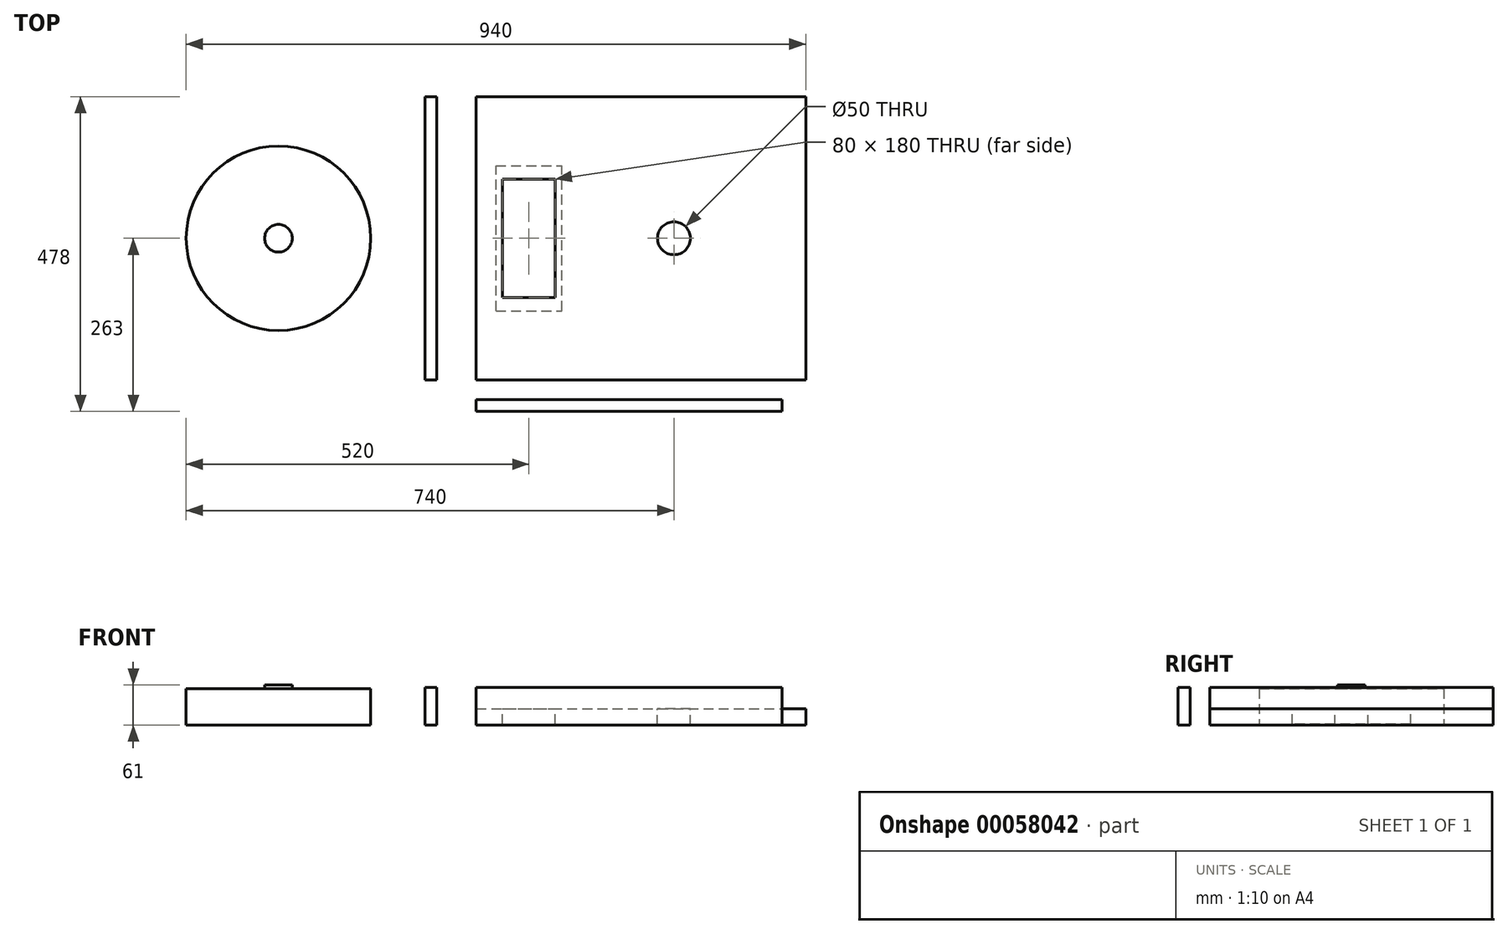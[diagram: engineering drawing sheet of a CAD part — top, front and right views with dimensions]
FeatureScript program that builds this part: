
annotation { "Feature Type Name" : "Feature", "Feature Type Description" : "" }
export const myFeature = defineFeature(function(context is Context, id is Id, definition is map)
    precondition{}
    {
        {
            var Q0;
            Q0=qCreatedBy(makeId("Top.planeOp"),FACE);
            var sketch = newSketch(context, id + "F0", { "sketchPlane" : qUnion([Q0])});
            skLineSegment(sketch, "E0.bottom", {"start": v(0, 0) * mm, "end": v(500, 0) * mm});
            skLineSegment(sketch, "E0.top", {"start": v(0, 430) * mm, "end": v(500, 430) * mm});
            skLineSegment(sketch, "E0.left", {"start": v(0, 0) * mm, "end": v(0, 430) * mm});
            skLineSegment(sketch, "E0.right", {"start": v(500, 0) * mm, "end": v(500, 430) * mm});
            skSolve(sketch);
        }
        {
            var Q0;
            Q0=makeQuery(id+"F0.imprint","IMPRINT",FACE,{"disambiguationData":[TD([[makeQuery(id+"F0.imprint","IMPRINT",EDGE,{"derivedFrom":sQuery(id+"F0.wireOp",EDGE,"E0.bottom")}),1.0]])]});
            extrude(context, id + "F1", {"entities" : qUnion([Q0]), "depth" : 25 * mm});
        }
        {
            var Q0;
            Q0=makeQuery(id+"F1.opExtrude","CAP_FACE",FACE,{"disambiguationData":[OSD([sQuery(id+"F0.wireOp",EDGE,"E0.bottom"),sQuery(id+"F0.wireOp",EDGE,"E0.top"),sQuery(id+"F0.wireOp",EDGE,"E0.left"),sQuery(id+"F0.wireOp",EDGE,"E0.right")])],"isStart":false});
            var sketch = newSketch(context, id + "F2", { "sketchPlane" : qUnion([Q0])});
            skLineSegment(sketch, "E1.bottom", {"start": v(40, 305) * mm, "end": v(120, 305) * mm});
            skLineSegment(sketch, "E1.top", {"start": v(40, 125) * mm, "end": v(120, 125) * mm});
            skLineSegment(sketch, "E1.left", {"start": v(40, 305) * mm, "end": v(40, 125) * mm});
            skLineSegment(sketch, "E1.right", {"start": v(120, 305) * mm, "end": v(120, 125) * mm});
            skCircle(sketch, "E2", {"center": v(300, 215) * mm, "radius": 25 * mm});
            skSolve(sketch);
        }
        {
            var Q0;
            Q0=qCreatedBy(makeId("Top.planeOp"),FACE);
            var sketch = newSketch(context, id + "F3", { "sketchPlane" : qUnion([Q0])});
            skCircle(sketch, "E3", {"center": v(-300, 215) * mm, "radius": 140 * mm});
            skSolve(sketch);
        }
        {
            var Q0;
            Q0=makeQuery(id+"F3.imprint","IMPRINT",FACE,{"disambiguationData":[TD([[makeQuery(id+"F3.imprint","IMPRINT",EDGE,{"derivedFrom":sQuery(id+"F3.wireOp",EDGE,"E3")}),1.0]])]});
            extrude(context, id + "F4", {"entities" : qUnion([Q0]), "depth" : 55 * mm});
        }
        {
            var Q0;
            Q0=makeQuery(id+"F4.opExtrude","CAP_FACE",FACE,{"disambiguationData":[OSD([sQuery(id+"F3.wireOp",EDGE,"E3")])],"isStart":false});
            var sketch = newSketch(context, id + "F5", { "sketchPlane" : qUnion([Q0])});
            skCircle(sketch, "E4", {"center": v(-300, 215) * mm, "radius": 21 * mm});
            skSolve(sketch);
        }
        {
            var Q0;
            Q0=makeQuery(id+"F5.imprint","IMPRINT",FACE,{"disambiguationData":[TD([[makeQuery(id+"F5.imprint","IMPRINT",EDGE,{"derivedFrom":sQuery(id+"F5.wireOp",EDGE,"E4")}),1.0]])]});
            extrude(context, id + "F6", {"entities" : qUnion([Q0]), "operationType" : NewBodyOperationType.ADD, "depth" : 6 * mm});
        }
        {
            var Q0;
            Q0=qCreatedBy(makeId("Top.planeOp"),FACE);
            var sketch = newSketch(context, id + "F7", { "sketchPlane" : qUnion([Q0])});
            skLineSegment(sketch, "E5.bottom", {"start": v(-78, 430) * mm, "end": v(-60, 430) * mm});
            skLineSegment(sketch, "E5.top", {"start": v(-78, 0) * mm, "end": v(-60, 0) * mm});
            skLineSegment(sketch, "E5.left", {"start": v(-78, 430) * mm, "end": v(-78, 0) * mm});
            skLineSegment(sketch, "E5.right", {"start": v(-60, 430) * mm, "end": v(-60, 0) * mm});
            skLineSegment(sketch, "E6.bottom", {"start": v(0, -30) * mm, "end": v(464, -30) * mm});
            skLineSegment(sketch, "E6.top", {"start": v(0, -48) * mm, "end": v(464, -48) * mm});
            skLineSegment(sketch, "E6.left", {"start": v(0, -30) * mm, "end": v(0, -48) * mm});
            skLineSegment(sketch, "E6.right", {"start": v(464, -30) * mm, "end": v(464, -48) * mm});
            skSolve(sketch);
        }
        {
            var Q0;
            Q0 = qSketchRegion(id + "F7", true);
            extrude(context, id + "F8", {"entities" : qUnion([Q0]), "depth" : 57 * mm});
        }
        {
            var Q0;
            Q0 = qSketchRegion(id + "F2", true);
            extrude(context, id + "F9", {"entities" : qUnion([Q0]), "operationType" : NewBodyOperationType.REMOVE, "endBound" : BoundingType.THROUGH_ALL, "oppositeDirection" : true, "depth" : 25 * mm});
        }
        {
            var Q0;
            Q0=makeQuery(id+"F1.opExtrude","CAP_FACE",FACE,{"disambiguationData":[OSD([sQuery(id+"F0.wireOp",EDGE,"E0.bottom"),sQuery(id+"F0.wireOp",EDGE,"E0.top"),sQuery(id+"F0.wireOp",EDGE,"E0.left"),sQuery(id+"F0.wireOp",EDGE,"E0.right")])],"isStart":true});
            var sketch = newSketch(context, id + "F10", { "sketchPlane" : qUnion([Q0])});
            skLineSegment(sketch, "E7.bottom", {"start": v(30, -105) * mm, "end": v(130, -105) * mm});
            skLineSegment(sketch, "E7.top", {"start": v(30, -325) * mm, "end": v(130, -325) * mm});
            skLineSegment(sketch, "E7.left", {"start": v(30, -105) * mm, "end": v(30, -325) * mm});
            skLineSegment(sketch, "E7.right", {"start": v(130, -105) * mm, "end": v(130, -325) * mm});
            skSolve(sketch);
        }
        {
            var Q0;
            Q0=makeQuery(id+"F10.imprint","IMPRINT",FACE,{"disambiguationData":[TD([[makeQuery(id+"F10.imprint","IMPRINT",EDGE,{"derivedFrom":sQuery(id+"F10.wireOp",EDGE,"E7.bottom")}),-1.0]])]});
            extrude(context, id + "F11", {"entities" : qUnion([Q0]), "operationType" : NewBodyOperationType.REMOVE, "oppositeDirection" : true, "depth" : 1.5 * mm});
        }
    });
